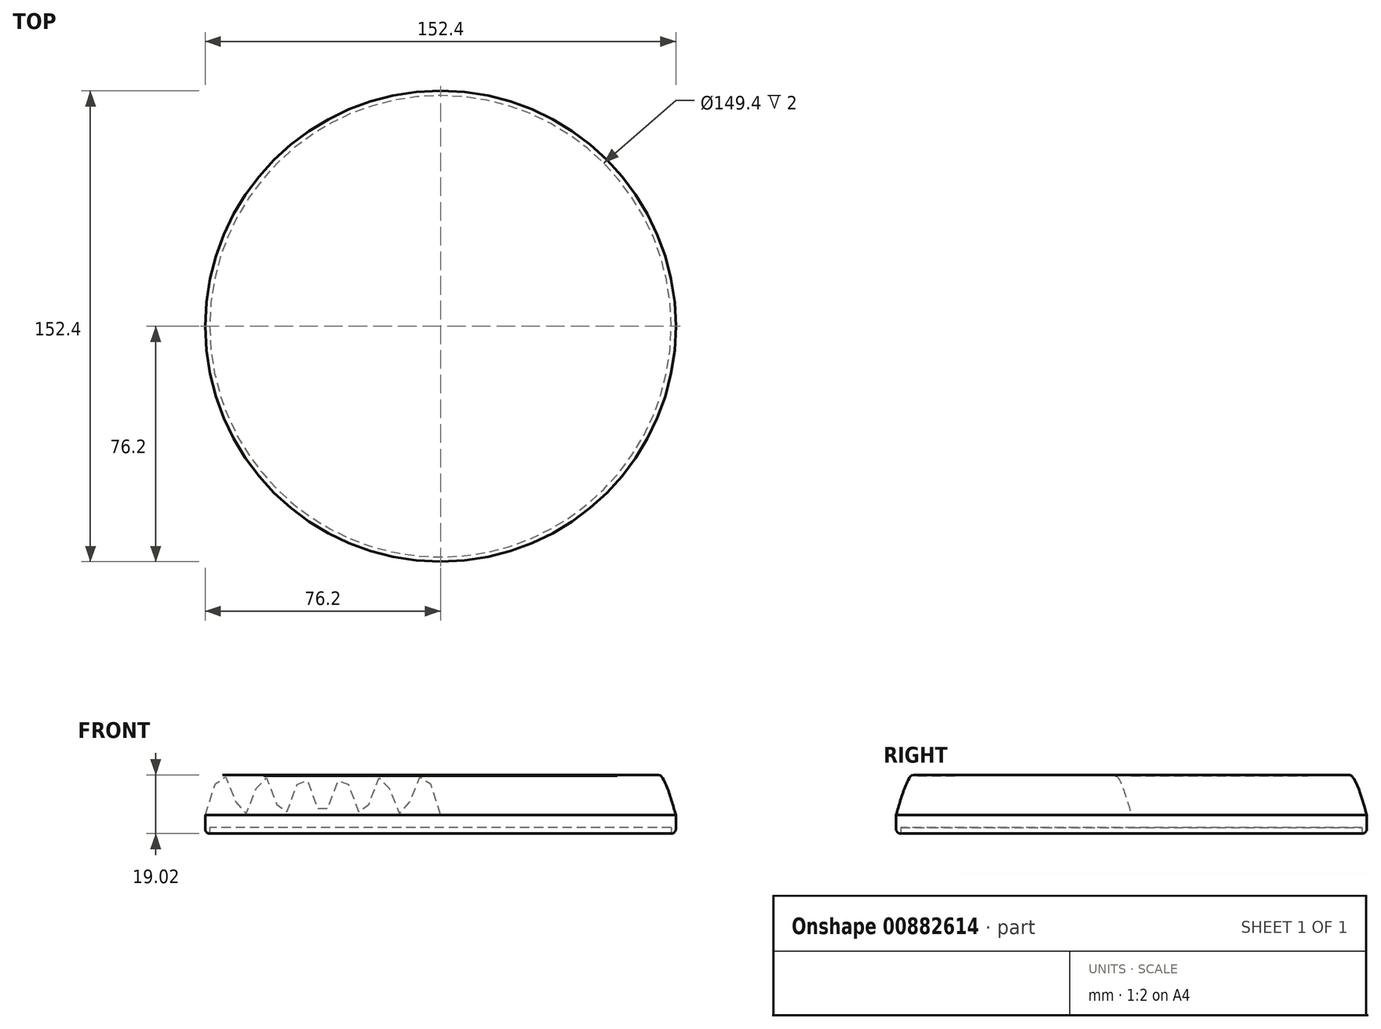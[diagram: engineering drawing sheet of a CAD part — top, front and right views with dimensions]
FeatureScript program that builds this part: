
annotation { "Feature Type Name" : "Feature", "Feature Type Description" : "" }
export const myFeature = defineFeature(function(context is Context, id is Id, definition is map)
    precondition{}
    {
        {
            var Q0;
            Q0=qCreatedBy(makeId("Front.planeOp"),FACE);
            var sketch = newSketch(context, id + "F0", { "sketchPlane" : qUnion([Q0])});
            skLineSegment(sketch, "E0", {"start": v(-63.5, 0) * mm, "end": v(-50.8, 0) * mm});
            skLineSegment(sketch, "E1", {"start": v(-50.8, 0) * mm, "end": v(-38.1, 0) * mm});
            skLineSegment(sketch, "E2", {"start": v(-38.1, 0) * mm, "end": v(-25.4, 0) * mm});
            skLineSegment(sketch, "E3", {"start": v(-25.4, 0) * mm, "end": v(-12.7, 0) * mm});
            skLineSegment(sketch, "E4", {"start": v(-12.7, 0) * mm, "end": v(0, 0) * mm});
            skLineSegment(sketch, "E5", {"start": v(-63.5, 0) * mm, "end": v(-76.2, 0) * mm});
            skPoint(sketch, "E6", {"position": v(-69.85, 0) * mm});
            skPoint(sketch, "E7", {"position": v(-57.15, 0) * mm});
            skPoint(sketch, "E8", {"position": v(-44.45, 0) * mm});
            skPoint(sketch, "E9", {"position": v(-31.75, 0) * mm});
            skPoint(sketch, "E10", {"position": v(-19.05, 0) * mm});
            skPoint(sketch, "E11", {"position": v(-6.35, 0) * mm});
            skPoint(sketch, "E12", {"position": v(-6.35, 12.7) * mm});
            skPoint(sketch, "E13", {"position": v(-19.05, 12.7) * mm});
            skPoint(sketch, "E14", {"position": v(-31.75, 12.7) * mm});
            skPoint(sketch, "E15", {"position": v(-44.45, 12.7) * mm});
            skPoint(sketch, "E16", {"position": v(-57.15, 12.7) * mm});
            skPoint(sketch, "E17", {"position": v(-69.85, 12.7) * mm});
            skFitSpline(sketch, "E18", {"points": [v(-76.2, 0) * mm, v(-69.85, 12.7) * mm, v(-63.5, 0) * mm, v(-57.15, 12.7) * mm, v(-50.8, 0) * mm, v(-44.45, 12.7) * mm, v(-38.1, 0) * mm, v(-31.75, 12.7) * mm, v(-25.4, 0) * mm, v(-19.05, 12.7) * mm, v(-12.7, 0) * mm, v(-6.35, 12.7) * mm, v(0, 0) * mm], "startDerivative": vector(76.2, 263.96) * mm, "endDerivative": vector(76.2, -263.96) * mm});
            skPoint(sketch, "E19", {"position": v(-76.2, 6) * mm});
            skPoint(sketch, "E20", {"position": v(-69.85, 18.7) * mm});
            skPoint(sketch, "E21", {"position": v(-63.5, 6) * mm});
            skPoint(sketch, "E22", {"position": v(-57.15, 18.7) * mm});
            skPoint(sketch, "E23", {"position": v(-50.8, 6) * mm});
            skPoint(sketch, "E24", {"position": v(-44.45, 18.7) * mm});
            skPoint(sketch, "E25", {"position": v(-31.75, 18.7) * mm});
            skPoint(sketch, "E26", {"position": v(-25.4, 6) * mm});
            skPoint(sketch, "E27", {"position": v(-19.05, 18.7) * mm});
            skPoint(sketch, "E28", {"position": v(-12.7, 6) * mm});
            skPoint(sketch, "E29", {"position": v(-6.35, 18.7) * mm});
            skFitSpline(sketch, "E30", {"points": [v(-76.2, 6) * mm, v(-69.85, 18.7) * mm, v(-63.5, 6) * mm, v(-57.15, 18.7) * mm, v(-50.8, 6) * mm, v(-44.45, 18.7) * mm, v(-38.1, 6) * mm, v(-31.75, 18.7) * mm, v(-25.4, 6) * mm, v(-19.05, 18.7) * mm, v(-12.7, 6) * mm, v(-6.35, 18.7) * mm, v(0, 6) * mm], "startDerivative": vector(76.2, 263.96) * mm, "endDerivative": vector(76.2, -263.96) * mm});
            skLineSegment(sketch, "E31", {"start": v(-76.2, 6) * mm, "end": v(-76.2, 0) * mm});
            skLineSegment(sketch, "E32", {"start": v(0, 6) * mm, "end": v(0, 0) * mm});
            skSolve(sketch);
        }
        {
            var Q0;
            Q0=qCreatedBy(makeId("Front.planeOp"),FACE);
            var sketch = newSketch(context, id + "F1", { "sketchPlane" : qUnion([Q0])});
            skLineSegment(sketch, "E33", {"start": v(0, 0) * mm, "end": v(0, 47.08) * mm, "construction": true});
            skSolve(sketch);
        }
        {
            var Q0;
            Q0=makeQuery(id+"F0.imprint","IMPRINT",FACE,{"disambiguationData":[TD([[makeQuery(id+"F0.imprint","IMPRINT",EDGE,{"derivedFrom":sQuery(id+"F0.wireOp",EDGE,"E30")}),-1.0]])]});
            var Q1;
            {var subQ0=sQuery(id+"F0.wireOp",EDGE,"E18");var subQ1=sQuery(id+"F0.wireOp",EDGE,"E5");var subQ3=makeQuery(id+"F0.imprint","INTERSECT",VERTEX,{"derivedFrom":[subQ1,subQ0]});Q1=makeQuery(id+"F0.imprint","IMPRINT",FACE,{"disambiguationData":[TD([[makeQuery(id+"F0.imprint","IMPRINT",EDGE,{"disambiguationData":[TD([[subQ3,-1.0]])],"derivedFrom":subQ1}),-1.0]])]});}
            var Q2;
            {var subQ0=sQuery(id+"F0.wireOp",EDGE,"E0");Q2=makeQuery(id+"F0.imprint","IMPRINT",FACE,{"disambiguationData":[TD([[makeQuery(id+"F0.imprint","IMPRINT",EDGE,{"derivedFrom":subQ0}),1.0]])]});}
            var Q3;
            {var subQ0=sQuery(id+"F0.wireOp",EDGE,"E1");Q3=makeQuery(id+"F0.imprint","IMPRINT",FACE,{"disambiguationData":[TD([[makeQuery(id+"F0.imprint","IMPRINT",EDGE,{"derivedFrom":subQ0}),1.0]])]});}
            var Q4;
            {var subQ0=sQuery(id+"F0.wireOp",EDGE,"E2");Q4=makeQuery(id+"F0.imprint","IMPRINT",FACE,{"disambiguationData":[TD([[makeQuery(id+"F0.imprint","IMPRINT",EDGE,{"derivedFrom":subQ0}),1.0]])]});}
            var Q5;
            {var subQ0=sQuery(id+"F0.wireOp",EDGE,"E3");Q5=makeQuery(id+"F0.imprint","IMPRINT",FACE,{"disambiguationData":[TD([[makeQuery(id+"F0.imprint","IMPRINT",EDGE,{"derivedFrom":subQ0}),1.0]])]});}
            var Q6;
            {var subQ0=sQuery(id+"F0.wireOp",EDGE,"E18");var subQ1=sQuery(id+"F0.wireOp",EDGE,"E4");var subQ3=makeQuery(id+"F0.imprint","INTERSECT",VERTEX,{"derivedFrom":[subQ1,subQ0]});Q6=makeQuery(id+"F0.imprint","IMPRINT",FACE,{"disambiguationData":[TD([[makeQuery(id+"F0.imprint","IMPRINT",EDGE,{"disambiguationData":[TD([[subQ3,-1.0]])],"derivedFrom":subQ1}),1.0]])]});}
            var Q7;
            Q7=sQuery(id+"F1.wireOp",EDGE,"E33");
            revolve(context, id + "F2", {"surfaceOperationType" : NewSurfaceOperationType.NEW, "entities" : qUnion([Q0, Q1, Q2, Q3, Q4, Q5, Q6]), "axis" : qUnion([Q7]), "revolveType" : RevolveType.FULL});
        }
        {
            var Q0;
            Q0=makeQuery(id+"F2.opRevolve","SWEPT_EDGE",EDGE,{"disambiguationData":[OSD([sQuery(id+"F0.wireOp",EDGE,"E5"),sQuery(id+"F0.wireOp",EDGE,"E18"),sQuery(id+"F0.wireOp",EDGE,"E31")])]});
            fillet(context, id + "F3", {"entities" : qUnion([Q0]), "radius" : 1.5 * mm, "tangentPropagation" : true, "allowEdgeOverflow" : false});
        }
        {
            var Q0;
            Q0=qCreatedBy(makeId("Top.planeOp"),FACE);
            var sketch = newSketch(context, id + "F4", { "sketchPlane" : qUnion([Q0])});
            skLineSegment(sketch, "E34", {"start": v(0, 19.05) * mm, "end": v(0, 0) * mm});
            skLineSegment(sketch, "E35.MirrorCS", {"start": v(0, -19.05) * mm, "end": v(0, 0) * mm});
            skArc(sketch, "E36", {"start": v(0, -19.05) * mm, "mid": v(19.04, 0) * mm, "end": v(0, 19.05) * mm});
            skArc(sketch, "E37", {"start": v(0, -19.05) * mm, "mid": v(4.42, 0) * mm, "end": v(0, 19.05) * mm});
            skPoint(sketch, "E38", {"position": v(11.73, 0) * mm});
            skCircle(sketch, "E39", {"center": v(0, 0) * mm, "radius": 25.4 * mm});
            skCircle(sketch, "E40.0", {"center": v(0, 0) * mm, "radius": 20.83 * mm});
            skCircle(sketch, "E41.0", {"center": v(0, 0) * mm, "radius": 19.03 * mm});
            skArc(sketch, "E42.0", {"start": v(7.33, -12.48) * mm, "mid": v(8.99, 0) * mm, "end": v(7.33, 12.48) * mm});
            skArc(sketch, "E42.1", {"start": v(7.33, -12.48) * mm, "mid": v(14.47, 0) * mm, "end": v(7.33, 12.48) * mm});
            skLineSegment(sketch, "E43", {"start": v(11.95, -1.97) * mm, "end": v(11.73, 1.45) * mm});
            skCircle(sketch, "E44", {"center": v(11.84, -0.26) * mm, "radius": 1.72 * mm});
            skArc(sketch, "E45", {"start": v(23.8, -8.86) * mm, "mid": v(19.2, -3.15) * mm, "end": v(11.95, -1.97) * mm});
            skArc(sketch, "E46", {"start": v(24.89, -5.07) * mm, "mid": v(19.36, 0.32) * mm, "end": v(11.73, 1.45) * mm});
            skCircle(sketch, "E47", {"center": v(11.84, -0.26) * mm, "radius": 2.27 * mm});
            skSolve(sketch);
        }
        {
            var Q0;
            {var subQ0=sQuery(id+"F4.wireOp",EDGE,"E35.MirrorCS");var subQ1=sQuery(id+"F4.wireOp",EDGE,"E34");var subQ2=makeQuery(id+"F4.imprint","INTERSECT",VERTEX,{"derivedFrom":[subQ1,subQ0]});Q0=makeQuery(id+"F4.imprint","IMPRINT",FACE,{"disambiguationData":[TD([[makeQuery(id+"F4.imprint","IMPRINT",EDGE,{"disambiguationData":[TD([[subQ2,1.0]])],"derivedFrom":subQ1}),-1.0]])]});}
            var Q1;
            {var subQ1=sQuery(id+"F4.wireOp",EDGE,"E34");var subQ6=sQuery(id+"F4.wireOp",EDGE,"E35.MirrorCS");var subQ7=makeQuery(id+"F4.imprint","INTERSECT",VERTEX,{"derivedFrom":[subQ1,subQ6]});Q1=makeQuery(id+"F4.imprint","IMPRINT",FACE,{"disambiguationData":[TD([[makeQuery(id+"F4.imprint","IMPRINT",EDGE,{"disambiguationData":[TD([[subQ7,1.0]])],"derivedFrom":subQ1}),1.0]])]});}
            var Q2;
            {var subQ5=sQuery(id+"F4.wireOp",EDGE,"E42.0");Q2=makeQuery(id+"F4.imprint","IMPRINT",FACE,{"disambiguationData":[TD([[makeQuery(id+"F4.imprint","IMPRINT",EDGE,{"derivedFrom":subQ5}),-1.0]])]});}
            var Q3;
            {var subQ8=sQuery(id+"F4.wireOp",EDGE,"E45");var subQ12=sQuery(id+"F4.wireOp",EDGE,"E40.0");var subQ13=makeQuery(id+"F4.imprint","INTERSECT",VERTEX,{"derivedFrom":[subQ12,subQ8]});Q3=makeQuery(id+"F4.imprint","IMPRINT",FACE,{"disambiguationData":[TD([[makeQuery(id+"F4.imprint","IMPRINT",EDGE,{"disambiguationData":[TD([[subQ13,1.0]])],"derivedFrom":subQ12}),1.0]])]});}
            var Q4;
            Q4=makeQuery(id+"F2.opRevolve","SWEPT_FACE",FACE,{"disambiguationData":[OSD([sQuery(id+"F0.wireOp",EDGE,"E1"),sQuery(id+"F0.wireOp",EDGE,"E2")])]});
            extrude(context, id + "F5", {"entities" : qUnion([Q0, Q1, Q2, Q3, Q4]), "operationType" : NewBodyOperationType.REMOVE, "depth" : 2 * mm, "offsetDistance" : 25.4 * mm});
        }
    });
